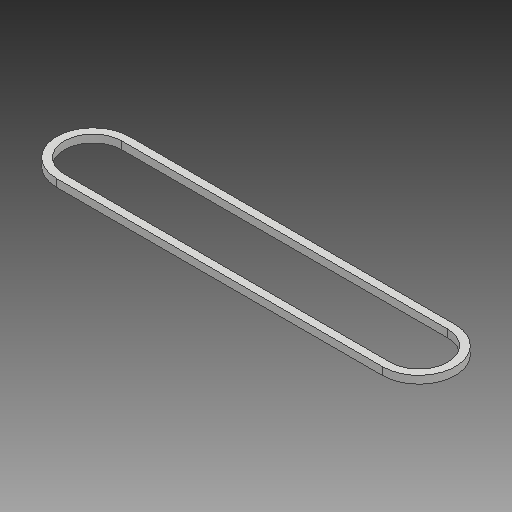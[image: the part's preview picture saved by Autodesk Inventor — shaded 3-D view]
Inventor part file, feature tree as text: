
AUTODESK INVENTOR PART (.ipt)
format: ipt  version: 2017 (Build 210142000, 142)  size: 105,984 bytes
history: native  units: mm
features: other x4, reference x2, extrude x1, sketch x1
ambient origin geometry x8: Origin, YZ Plane, XZ Plane, XY Plane, X Axis, Y Axis, Z Axis, Center Point
bodies: Solid1 (feature_tree)
feature tree (8):
  extrude  "Extrusion1"  Depth=8.0mm TaperAngle=0.0deg
  sketch  "Sketch1"  dims[d0=8.0mm d1=8.0mm d2=0.0mm]
  reference  "Reference1"
  reference  "Reference2"
  other  "<userpath>\OneDrive\Inventor\VolledigGeassembleerdv001.iam"
  other  "VolledigGeassembleerdv001.iam"
  other  "kettingwiel:1"
  other  "kettingwiel:2"
